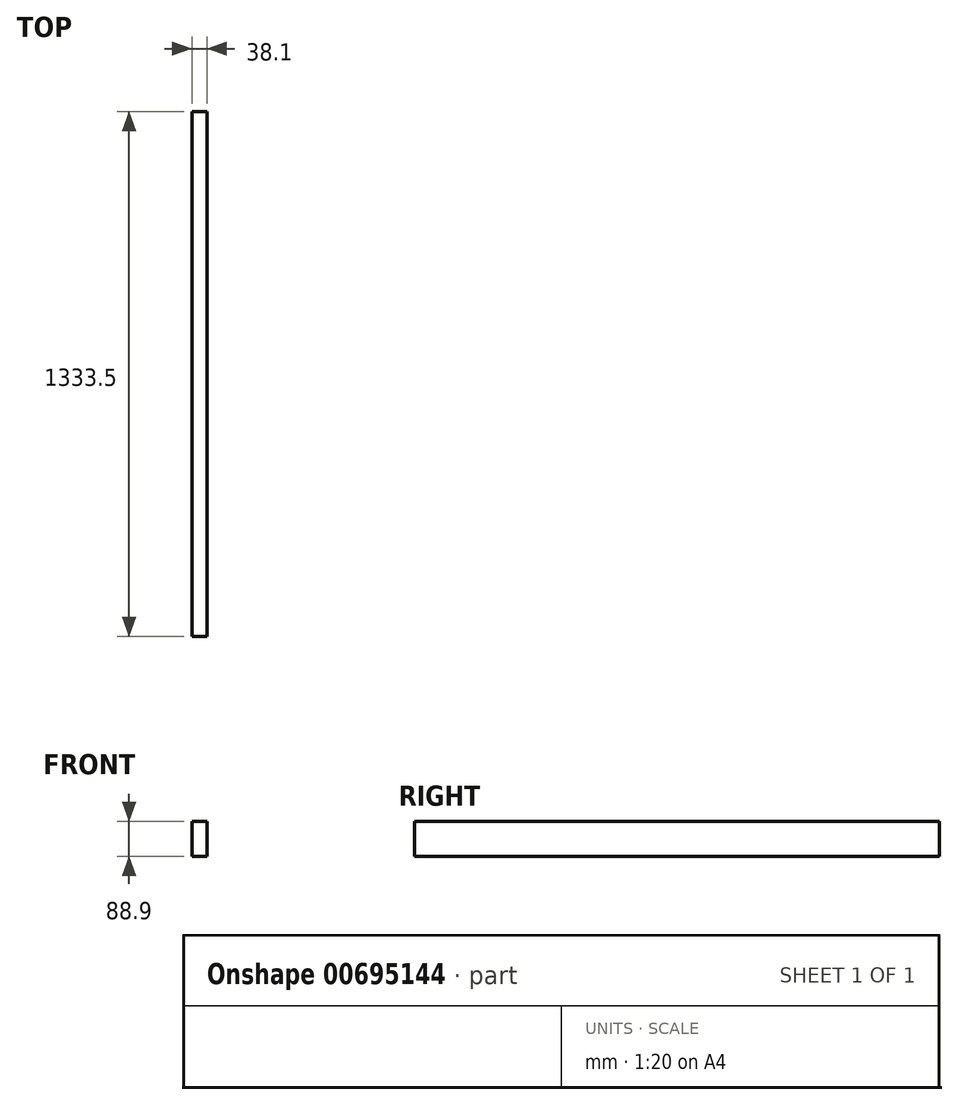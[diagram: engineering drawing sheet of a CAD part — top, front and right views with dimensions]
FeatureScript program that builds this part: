
annotation { "Feature Type Name" : "Feature", "Feature Type Description" : "" }
export const myFeature = defineFeature(function(context is Context, id is Id, definition is map)
    precondition{}
    {
        {
            var Q0;
            Q0=qCreatedBy(makeId("Front.planeOp"),FACE);
            var sketch = newSketch(context, id + "F0", { "sketchPlane" : qUnion([Q0])});
            skLineSegment(sketch, "E0.bottom", {"start": v(-100.3, 646.2) * mm, "end": v(-62.2, 646.2) * mm});
            skLineSegment(sketch, "E0.top", {"start": v(-100.3, 557.3) * mm, "end": v(-62.2, 557.3) * mm});
            skLineSegment(sketch, "E0.left", {"start": v(-100.3, 646.2) * mm, "end": v(-100.3, 557.3) * mm});
            skLineSegment(sketch, "E0.right", {"start": v(-62.2, 646.2) * mm, "end": v(-62.2, 557.3) * mm});
            skSolve(sketch);
        }
        {
            var Q0;
            Q0=makeQuery(id+"F0.imprint","IMPRINT",FACE,{"disambiguationData":[TD([[makeQuery(id+"F0.imprint","IMPRINT",EDGE,{"derivedFrom":sQuery(id+"F0.wireOp",EDGE,"E0.bottom")}),-1.0]])]});
            extrude(context, id + "F1", {"entities" : qUnion([Q0]), "depth" : 1333.5 * mm, "offsetDistance" : 25.4 * mm});
        }
    });
